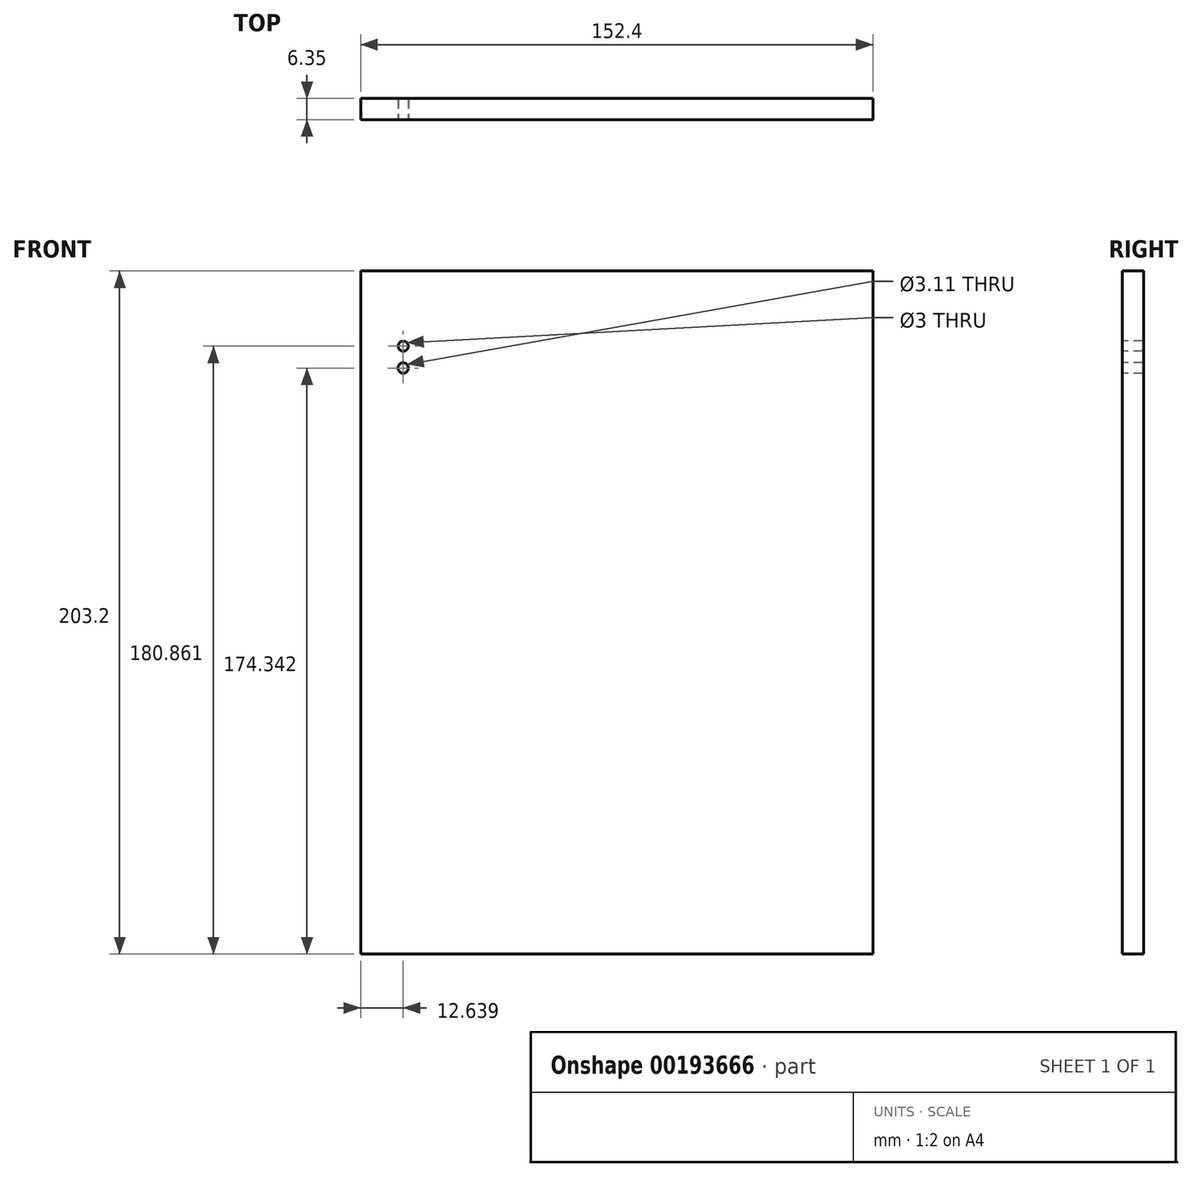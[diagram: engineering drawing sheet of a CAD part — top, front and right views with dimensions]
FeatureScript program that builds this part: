
annotation { "Feature Type Name" : "Feature", "Feature Type Description" : "" }
export const myFeature = defineFeature(function(context is Context, id is Id, definition is map)
    precondition{}
    {
        {
            var Q0;
            Q0=qCreatedBy(makeId("Front.planeOp"),FACE);
            var sketch = newSketch(context, id + "F0", { "sketchPlane" : qUnion([Q0])});
            skLineSegment(sketch, "E0.bottom", {"start": v(76.2, 101.6) * mm, "end": v(-76.2, 101.6) * mm});
            skLineSegment(sketch, "E0.top", {"start": v(76.2, -101.6) * mm, "end": v(-76.2, -101.6) * mm});
            skLineSegment(sketch, "E0.left", {"start": v(76.2, 101.6) * mm, "end": v(76.2, -101.6) * mm});
            skLineSegment(sketch, "E0.right", {"start": v(-76.2, 101.6) * mm, "end": v(-76.2, -101.6) * mm});
            skPoint(sketch, "E0.middle", {"position": v(0, 0) * mm});
            skSolve(sketch);
        }
        {
            var Q0;
            Q0=makeQuery(id+"F0.imprint","IMPRINT",FACE,{"disambiguationData":[TD([[makeQuery(id+"F0.imprint","IMPRINT",EDGE,{"derivedFrom":sQuery(id+"F0.wireOp",EDGE,"E0.bottom")}),1.0]])]});
            extrude(context, id + "F1", {"entities" : qUnion([Q0]), "depth" : 6.35 * mm});
        }
        {
            var Q0;
            Q0=makeQuery(id+"F1.opExtrude","CAP_FACE",FACE,{"disambiguationData":[OSD([sQuery(id+"F0.wireOp",EDGE,"E0.bottom"),sQuery(id+"F0.wireOp",EDGE,"E0.top"),sQuery(id+"F0.wireOp",EDGE,"E0.left"),sQuery(id+"F0.wireOp",EDGE,"E0.right")])],"isStart":false});
            var sketch = newSketch(context, id + "F2", { "sketchPlane" : qUnion([Q0])});
            skLineSegment(sketch, "E1", {"start": v(-63.5, 101.6) * mm, "end": v(-63.5, 82.55) * mm});
            skLineSegment(sketch, "E2", {"start": v(-63.5, 82.55) * mm, "end": v(-63.5, 69.85) * mm});
            skSolve(sketch);
        }
        {
            var Q0;
            Q0=makeQuery(id+"F2.imprint","IMPRINT",FACE,{"disambiguationData":[TD([[makeQuery(id+"F2.imprint","IMPRINT",EDGE,{"derivedFrom":makeQuery(id+"F1.opExtrude","CAP_EDGE",EDGE,{"disambiguationData":[OSD([sQuery(id+"F0.wireOp",EDGE,"E0.top")])],"isStart":false})}),-1.0]])]});
            var sketch = newSketch(context, id + "F3", { "sketchPlane" : qUnion([Q0])});
            skCircle(sketch, "E3", {"center": v(-63.56, 79.26) * mm, "radius": 1.5 * mm});
            skCircle(sketch, "E4", {"center": v(-63.56, 72.74) * mm, "radius": 1.56 * mm});
            skSolve(sketch);
        }
        {
            var Q0;
            Q0=makeQuery(id+"F3.imprint","IMPRINT",FACE,{"disambiguationData":[TD([[makeQuery(id+"F3.imprint","IMPRINT",EDGE,{"derivedFrom":sQuery(id+"F3.wireOp",EDGE,"E3")}),1.0]])]});
            var Q1;
            Q1=makeQuery(id+"F3.imprint","IMPRINT",FACE,{"disambiguationData":[TD([[makeQuery(id+"F3.imprint","IMPRINT",EDGE,{"derivedFrom":sQuery(id+"F3.wireOp",EDGE,"E4")}),1.0]])]});
            extrude(context, id + "F4", {"entities" : qUnion([Q0, Q1]), "operationType" : NewBodyOperationType.REMOVE, "oppositeDirection" : true, "depth" : 25.4 * mm});
        }
    });
